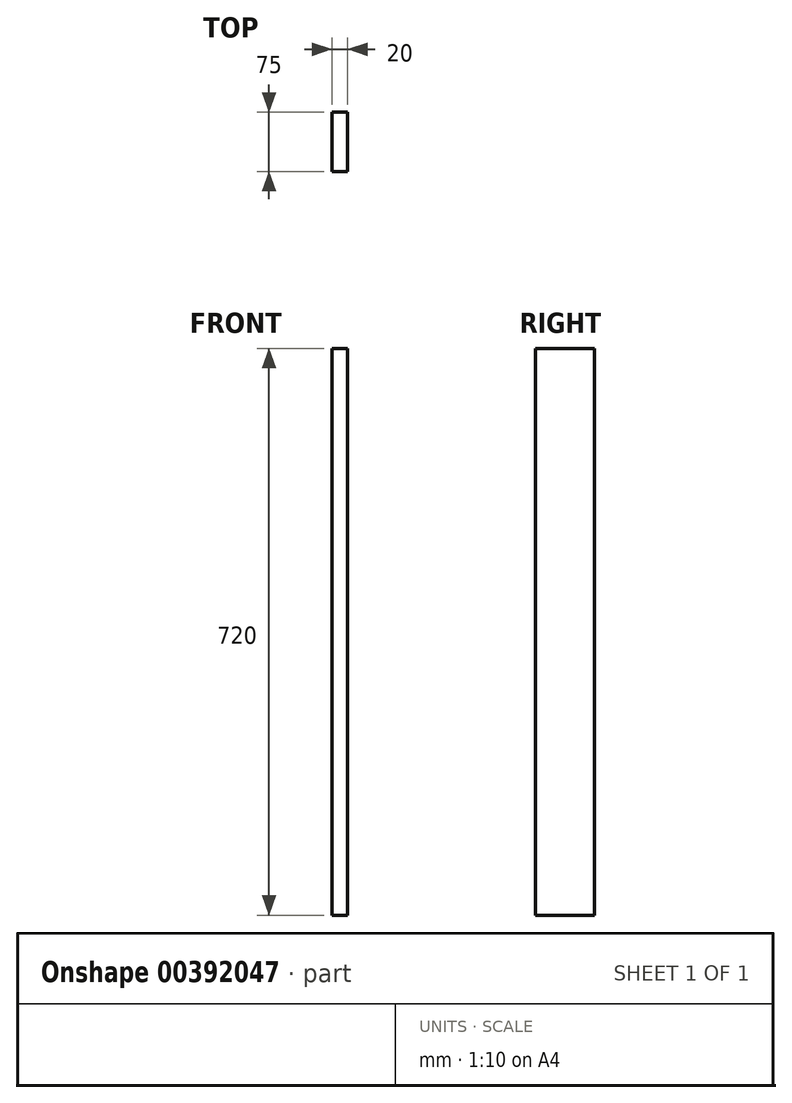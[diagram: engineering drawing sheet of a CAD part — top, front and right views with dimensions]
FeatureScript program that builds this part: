
annotation { "Feature Type Name" : "Feature", "Feature Type Description" : "" }
export const myFeature = defineFeature(function(context is Context, id is Id, definition is map)
    precondition{}
    {
        {
            var Q0;
            Q0=qCreatedBy(makeId("Top.planeOp"),FACE);
            var sketch = newSketch(context, id + "F0", { "sketchPlane" : qUnion([Q0])});
            skLineSegment(sketch, "E0.bottom", {"start": v(-10, 37.5) * mm, "end": v(10, 37.5) * mm});
            skLineSegment(sketch, "E0.top", {"start": v(-10, -37.5) * mm, "end": v(10, -37.5) * mm});
            skLineSegment(sketch, "E0.left", {"start": v(-10, 37.5) * mm, "end": v(-10, -37.5) * mm});
            skLineSegment(sketch, "E0.right", {"start": v(10, 37.5) * mm, "end": v(10, -37.5) * mm});
            skPoint(sketch, "E0.middle", {"position": v(0, 0) * mm});
            skSolve(sketch);
        }
        {
            var Q0;
            Q0 = qSketchRegion(id + "F0", true);
            extrude(context, id + "F1", {"entities" : qUnion([Q0]), "endBound" : BoundingType.SYMMETRIC, "depth" : 720 * mm});
        }
    });
